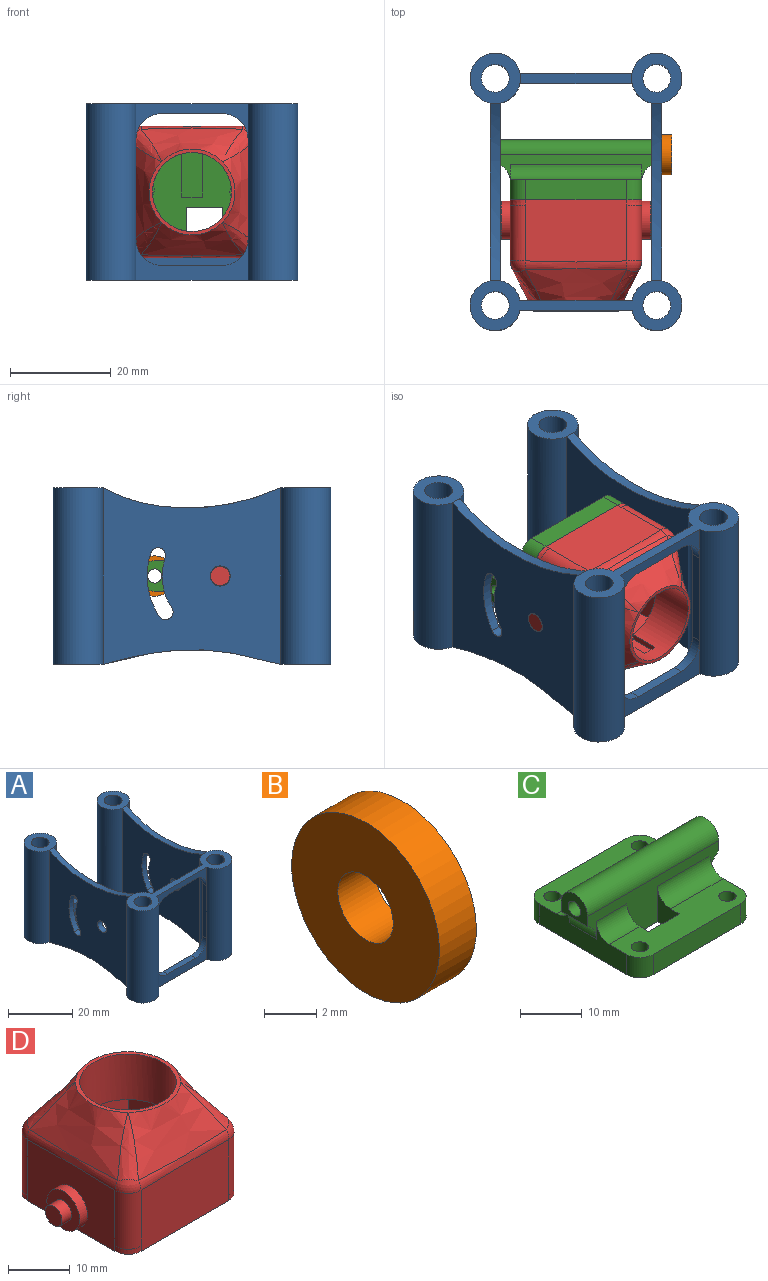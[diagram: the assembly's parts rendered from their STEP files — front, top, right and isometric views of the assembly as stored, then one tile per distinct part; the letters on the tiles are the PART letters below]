
ASSEMBLY  parts=4 mates=5
PART A: 48 faces, bbox 42x55x35 mm
  f0: plane 35.2x35mm, normal (1,0,0), area 1015.3mm2, adj f14,f16,f33,f34,f35,f40,f42,f44
  f1: plane 10x9.9mm, normal (0,0,1), area 54.6mm2, adj f15,f23,f43
  f2: plane 10x9.9mm, normal (0,0,1), area 54.6mm2, adj f16,f20,f42
  f3: plane 42x9.9mm, normal (0,0,1), area 153.4mm2, adj f12,f13,f14,f17,f18,f19,f21,f22
  f4: plane 35.2x35mm, normal (-1,0,0), area 1015.3mm2, adj f12,f15,f36,f37,f38,f41,f43,f46
  f5: plane 35.2x35mm, normal (1,0,0), area 1015.3mm2, adj f15,f22,f36,f37,f38,f41,f43,f46
  f6: plane 35.2x35mm, normal (-1,0,0), area 1015.3mm2, adj f16,f17,f33,f34,f35,f40,f42,f44
  f7: plane 42x9.9mm, normal (0,0,-1), area 153.4mm2, adj f8,f9,f15,f16,f20,f23,f40,f41
  f8: plane 22.2x5mm, normal (0,1,0), area 111mm2, adj f7,f15,f16,f39
  f9: plane 22.2x5mm, normal (0,-1,0), area 111mm2, adj f7,f15,f16,f39
  f10: plane 22.2x8mm, normal (0,-1,0), area 77.3mm2, adj f12,f14,f24,f28,f29,f30
  f11: plane 22.2x8mm, normal (0,1,0), area 77.3mm2, adj f17,f22,f24,f28,f29,f30
  f12: cylinder r=5mm len=35mm, axis (0,0,-1), area 754.2mm2, adj f3,f4,f10,f13,f24,f25
  f13: plane 22.2x7mm, normal (0,-1,0), area 55.1mm2, adj f3,f12,f14,f26,f27,f32
  f14: cylinder r=5mm len=35mm, axis (0,0,-1), area 754.2mm2, adj f0,f3,f10,f13,f24,f31
  f15: cylinder r=5mm len=35mm, axis (0,0,-1), area 1019mm2, adj f1,f4,f5,f7,f8,f9,f39
  f16: cylinder r=5mm len=35mm, axis (0,0,-1), area 1019mm2, adj f0,f2,f6,f7,f8,f9,f39
  f17: cylinder r=5mm len=35mm, axis (0,0,-1), area 204.4mm2, adj f3,f6,f11,f18,f24,f31
  f18: plane 22.2x7mm, normal (0,1,0), area 55.1mm2, adj f3,f17,f22,f26,f27,f32
  f19: cylinder r=2.75mm len=35mm, axis (0,0,-1), area 604.8mm2, adj f3,f24
  f20: cylinder r=2.75mm len=35mm, axis (0,0,-1), area 604.8mm2, adj f2,f7
  f21: cylinder r=2.75mm len=35mm, axis (0,0,-1), area 604.8mm2, adj f3,f24
  f22: cylinder r=5mm len=35mm, axis (0,0,-1), area 204.4mm2, adj f3,f5,f11,f18,f24,f25
  f23: cylinder r=2.75mm len=35mm, axis (0,0,-1), area 604.8mm2, adj f1,f7
  f24: plane 42x9.9mm, normal (0,0,-1), area 153.4mm2, adj f10,f11,f12,f14,f17,f19,f21,f22
  f25: plane 20x2mm, normal (1,0,0), area 40mm2, adj f12,f22,f27,f28
  f26: plane 12.2x2mm, normal (0,0,-1), area 24.4mm2, adj f13,f18,f27,f32
  f27: cylinder r=5mm len=5mm, axis (0,-1,0), area 15.7mm2, adj f13,f18,f25,f26
  f28: cylinder r=5mm len=5mm, axis (0,-1,0), area 15.7mm2, adj f10,f11,f25,f29
  f29: plane 12.2x2mm, normal (0,0,1), area 24.4mm2, adj f10,f11,f28,f30
  f30: cylinder r=5mm len=5mm, axis (0,-1,0), area 15.7mm2, adj f10,f11,f29,f31
  f31: plane 20x2mm, normal (-1,0,0), area 40mm2, adj f14,f17,f30,f32
  f32: cylinder r=5mm len=5mm, axis (0,-1,0), area 15.7mm2, adj f13,f18,f26,f31
  f33: cylinder r=14.5mm len=12.55mm, axis (1,0,0), area 26.2mm2, adj f0,f6,f44,f45
  f34: cylinder r=11.5mm len=9.95mm, axis (1,0,0), area 20.8mm2, adj f0,f6,f44,f45
  f35: cylinder r=2mm len=4mm, axis (1,0,0), area 25.1mm2, adj f0,f6
  f36: cylinder r=11.5mm len=9.95mm, axis (1,0,0), area 20.8mm2, adj f4,f5,f46,f47
  f37: cylinder r=14.5mm len=12.55mm, axis (1,0,0), area 26.2mm2, adj f4,f5,f46,f47
  f38: cylinder r=2mm len=4mm, axis (1,0,0), area 25.1mm2, adj f4,f5
  f39: plane 22.2x2mm, normal (0,0,1), area 44.1mm2, adj f8,f9,f15,f16
  f40: extruded ~35.2x2.91mm, area 71.6mm2, adj f0,f6,f7,f24
  f41: extruded ~35.2x2.91mm, area 71.6mm2, adj f4,f5,f7,f24
  f42: extruded ~35.2x4.01mm, area 72.9mm2, adj f0,f2,f3,f6
  f43: extruded ~35.2x4.01mm, area 72.9mm2, adj f1,f3,f4,f5
  f44: cylinder r=1.5mm len=2.75mm, axis (1,0,0), area 9.4mm2, adj f0,f6,f33,f34
  f45: cylinder r=1.5mm len=2.92mm, axis (1,0,0), area 9.4mm2, adj f0,f6,f33,f34
  f46: cylinder r=1.5mm len=2.75mm, axis (1,0,0), area 9.4mm2, adj f4,f5,f36,f37
  f47: cylinder r=1.5mm len=2.92mm, axis (1,0,0), area 9.4mm2, adj f4,f5,f36,f37
PART B: 4 faces, bbox 2x8x8 mm
  f0: cylinder r=1.5mm len=3mm, axis (-1,0,0), area 18.8mm2, adj f2,f3
  f1: cylinder r=4mm len=8mm, axis (-1,0,0), area 50.3mm2, adj f2,f3
  f2: plane 8x8mm, normal (1,0,0), area 43.2mm2, adj f0,f1
  f3: plane 8x8mm, normal (-1,0,0), area 43.2mm2, adj f0,f1
PART C: 38 faces, bbox 30x26x12 mm
  f0: plane 26x7mm, normal (0,0,1), area 151.8mm2, adj f3,f7,f8,f9,f10,f12,f13,f16
  f1: plane 26x26mm, normal (0,0,-1), area 533.4mm2, adj f3,f4,f5,f6,f7,f8,f9,f10
  f2: plane 26x7mm, normal (0,0,1), area 165.8mm2, adj f3,f4,f5,f6,f7,f11,f14,f30
  f3: plane 20x7mm, normal (1,0,0), area 81.1mm2, adj f0,f1,f2,f4,f10,f15,f28,f30
  f4: cylinder r=3mm len=4mm, axis (0,0,-1), area 18.8mm2, adj f1,f2,f3,f5
  f5: plane 20x4mm, normal (0,1,0), area 80mm2, adj f1,f2,f4,f6
  f6: cylinder r=3mm len=4mm, axis (0,0,-1), area 18.8mm2, adj f1,f2,f5,f7
  f7: plane 20x7mm, normal (-1,0,0), area 81.1mm2, adj f0,f1,f2,f6,f8,f15,f28,f29
  f8: cylinder r=3mm len=4mm, axis (0,0,-1), area 18.8mm2, adj f0,f1,f7,f9
  f9: plane 20x4mm, normal (0,-1,0), area 80mm2, adj f0,f1,f8,f10
  f10: cylinder r=3mm len=4mm, axis (0,0,-1), area 18.8mm2, adj f0,f1,f3,f9
  f11: cylinder r=1.4mm len=4mm, axis (0,0,1), area 35.2mm2, adj f1,f2
  f12: cylinder r=1.4mm len=4mm, axis (0,0,1), area 35.2mm2, adj f0,f1
  f13: cylinder r=1.4mm len=4mm, axis (0,0,1), area 35.2mm2, adj f0,f1
  f14: cylinder r=1.4mm len=4mm, axis (0,0,1), area 35.2mm2, adj f1,f2
  f15: plane 30x8.99mm, normal (0,-1,0), area 112.7mm2, adj f1,f3,f7,f16,f18,f29,f31,f32
  f16: plane 7x5mm, normal (1,0,0), area 21.9mm2, adj f0,f1,f15,f17,f29
  f17: plane 7x4mm, normal (0,1,0), area 28mm2, adj f0,f1,f16,f18
  f18: plane 7x5mm, normal (-1,0,0), area 21.9mm2, adj f0,f1,f15,f17,f31
  f19: cylinder r=2.5mm len=5mm, axis (0,0,-1), area 31.4mm2, adj f1,f20
  f20: plane 5x5mm, normal (0,0,-1), area 19.6mm2, adj f19
  f21: cylinder r=2.5mm len=5mm, axis (0,0,-1), area 31.4mm2, adj f1,f22
  f22: plane 5x5mm, normal (0,0,-1), area 19.6mm2, adj f21
  f23: plane 4x1mm, normal (0,-1,0), area 4mm2, adj f1,f24,f26,f27
  f24: plane 9x1mm, normal (-1,0,0), area 9mm2, adj f1,f23,f25,f27
  f25: plane 4x1mm, normal (0,1,0), area 4mm2, adj f1,f24,f26,f27
  f26: plane 9x1mm, normal (1,0,0), area 9mm2, adj f1,f23,f25,f27
  f27: plane 9x4mm, normal (0,0,-1), area 36mm2, adj f23,f24,f25,f26
  f28: plane 30x5.45mm, normal (0,1,0), area 63.7mm2, adj f3,f7,f30,f32,f33,f34,f35,f36
  f29: cylinder r=3mm len=7mm, axis (1,0,0), area 33mm2, adj f0,f7,f15,f16
  f30: cylinder r=3mm len=26mm, axis (-1,0,0), area 122.5mm2, adj f2,f3,f7,f28
  f31: cylinder r=3mm len=12mm, axis (1,0,0), area 56.5mm2, adj f0,f3,f15,f18
  f32: cylinder r=3mm len=30mm, axis (1,0,0), area 282.7mm2, adj f15,f28,f33,f34
  f33: plane 6x4.99mm, normal (-1,0,0), area 19.9mm2, adj f15,f28,f32,f36,f37
  f34: plane 6x4.99mm, normal (1,0,0), area 19.9mm2, adj f15,f28,f32,f35,f37
  f35: cylinder r=4mm len=6mm, axis (0,-1,0), area 25.1mm2, adj f3,f15,f28,f34
  f36: cylinder r=4mm len=6mm, axis (0,1,0), area 25.1mm2, adj f7,f15,f28,f33
  f37: cylinder r=1.4mm len=30mm, axis (1,0,0), area 263.9mm2, adj f33,f34
PART D: 66 faces, bbox 34x26x22 mm
  f0: plane 26x26mm, normal (0,0,-1), area 288.8mm2, adj f3,f4,f6,f7,f8,f9,f10,f12
  f1: plane 25.1x18mm, normal (0,0,-1), area 159.3mm2, adj f3,f4,f5,f6,f7,f8,f9,f10
  f2: sphere r=3mm, area 8mm2, adj f16,f19,f20,f21
  f3: plane 13x6.38mm, normal (1,0,0), area 82.9mm2, adj f0,f1,f4,f14
  f4: plane 13x0.88mm, normal (0,-1,0), area 11.4mm2, adj f0,f1,f3,f5,f44
  f5: cylinder r=2.62mm len=12mm, axis (0,0,1), area 99mm2, adj f1,f4,f6,f44
  f6: plane 13x0.88mm, normal (0,1,0), area 11.4mm2, adj f0,f1,f5,f7,f44
  f7: plane 13x6.38mm, normal (1,0,0), area 82.9mm2, adj f0,f1,f6,f8
  f8: plane 18x13mm, normal (0,1,0), area 234mm2, adj f0,f1,f7,f9
  f9: plane 13x6.38mm, normal (-1,0,0), area 82.9mm2, adj f0,f1,f8,f10
  f10: plane 13x0.88mm, normal (0,1,0), area 11.4mm2, adj f0,f1,f9,f11,f45
  f11: cylinder r=2.62mm len=12mm, axis (0,0,1), area 99mm2, adj f1,f10,f12,f45
  f12: plane 13x0.88mm, normal (0,-1,0), area 11.4mm2, adj f0,f1,f11,f13,f45
  f13: plane 13x6.38mm, normal (-1,0,0), area 82.9mm2, adj f0,f1,f12,f14
  f14: plane 18x13mm, normal (0,-1,0), area 234mm2, adj f0,f1,f3,f13
  f15: plane 20x12.29mm, normal (0,1,0), area 244.3mm2, adj f0,f16,f21,f22,f48,f49
  f16: cylinder r=3mm len=11.07mm, axis (0,0,-1), area 52.2mm2, adj f2,f15,f17,f49
  f17: plane 20x12.29mm, normal (1,0,0), area 200.1mm2, adj f0,f16,f18,f19,f46,f49,f50
  f18: cylinder r=3mm len=11.07mm, axis (0,0,-1), area 52.2mm2, adj f17,f23,f24,f46
  f19: bspline ~20.54x1.74mm, area 31mm2, adj f2,f17,f23,f26
  f20: bspline ~8.2x6.44mm, area 15.1mm2, adj f2,f26,f27
  f21: bspline ~20.54x1.74mm, area 31mm2, adj f2,f15,f27,f29
  f22: cylinder r=3mm len=11.07mm, axis (0,0,-1), area 52.2mm2, adj f15,f28,f29,f48
  f23: sphere r=3mm, area 8mm2, adj f18,f19,f30,f32
  f24: plane 20x12.29mm, normal (0,-1,0), area 244.3mm2, adj f0,f18,f31,f32,f46,f47
  f25: cylinder r=7.83mm len=15.65mm, axis (0,0,-1), area 424.4mm2, adj f1,f33,f40,f41,f42
  f26: bspline ~25.15x8.45mm, area 164.2mm2, adj f19,f20,f30,f33
  f27: bspline ~24.76x8.2mm, area 164.2mm2, adj f20,f21,f33,f34
  f28: plane 20x12.29mm, normal (-1,0,0), area 200.1mm2, adj f0,f22,f31,f35,f47,f48,f54
  f29: sphere r=3mm, area 8mm2, adj f21,f22,f34,f35
  f30: bspline ~8.2x6.44mm, area 15.1mm2, adj f23,f26,f36
  f31: cylinder r=3mm len=11.07mm, axis (0,0,-1), area 52.2mm2, adj f24,f28,f37,f47
  f32: bspline ~20.54x1.74mm, area 31mm2, adj f23,f24,f36,f37
  f33: plane 17.32x17.32mm, normal (0,0,1), area 34.6mm2, adj f25,f26,f27,f36,f38
  f34: revolved ~8.21x7.88mm, area 20mm2, adj f27,f29,f38
  f35: bspline ~20.54x1.74mm, area 31mm2, adj f28,f29,f37,f38
  f36: bspline ~25.15x8.45mm, area 164.2mm2, adj f30,f32,f33,f39
  f37: sphere r=3mm, area 8mm2, adj f31,f32,f35,f39
  f38: bspline ~24.76x8.2mm, area 164.2mm2, adj f33,f34,f35,f39
  f39: revolved ~8.21x7.88mm, area 20mm2, adj f36,f37,f38
  f40: plane 6x1.15mm, normal (-1,0,0), area 6.9mm2, adj f1,f25,f42,f43
  f41: plane 6x1.15mm, normal (1,0,0), area 6.9mm2, adj f1,f25,f42,f43
  f42: plane 3x1.15mm, normal (0,0,-1), area 3.1mm2, adj f25,f40,f41,f43
  f43: plane 6x3mm, normal (0,1,0), area 18mm2, adj f1,f40,f41,f42
  f44: extruded ~5.25x2.63mm, area 8.2mm2, adj f0,f4,f5,f6
  f45: extruded ~5.25x2.63mm, area 8.2mm2, adj f0,f10,f11,f12
  f46: extruded ~3x3mm, area 4.7mm2, adj f0,f17,f18,f24
  f47: extruded ~3x3mm, area 4.7mm2, adj f0,f24,f28,f31
  f48: extruded ~3x3mm, area 4.7mm2, adj f0,f15,f22,f28
  f49: extruded ~3x3mm, area 4.7mm2, adj f0,f15,f16,f17
  f50: cylinder r=3.75mm len=7.5mm, axis (-1,0,0), area 42.4mm2, adj f17,f51
  f51: plane 7.5x7.5mm, normal (1,0,0), area 32.8mm2, adj f50,f53
  f52: plane 3.8x3.8mm, normal (1,0,0), area 11.3mm2, adj f53
  f53: cylinder r=1.9mm len=3.8mm, axis (-1,0,0), area 26.3mm2, adj f51,f52
  f54: cylinder r=3.75mm len=7.5mm, axis (1,0,0), area 42.4mm2, adj f28,f55
  f55: plane 7.5x7.5mm, normal (-1,0,0), area 32.8mm2, adj f54,f57
  f56: plane 3.8x3.8mm, normal (-1,0,0), area 11.3mm2, adj f57
  f57: cylinder r=1.9mm len=3.8mm, axis (1,0,0), area 26.3mm2, adj f55,f56
  f58: cylinder r=1.4mm len=10mm, axis (0,0,-1), area 88mm2, adj f0,f59
  f59: plane 2.8x2.8mm, normal (0,0,-1), area 6.2mm2, adj f58
  f60: cylinder r=1.4mm len=10mm, axis (0,0,-1), area 88mm2, adj f0,f61
  f61: plane 2.8x2.8mm, normal (0,0,-1), area 6.2mm2, adj f60
  f62: cylinder r=1.4mm len=10mm, axis (0,0,-1), area 88mm2, adj f0,f63
  f63: plane 2.8x2.8mm, normal (0,0,-1), area 6.2mm2, adj f62
  f64: cylinder r=1.4mm len=10mm, axis (0,0,-1), area 88mm2, adj f0,f65
  f65: plane 2.8x2.8mm, normal (0,0,-1), area 6.2mm2, adj f64
PLACE A t=(1.71,45.47,-17.63)mm
PLACE B t=(16.55,51.13,-0.13)mm
PLACE C rot(axis=(0,-0.71,-0.71),180deg) t=(12.55,42.13,-13.13)mm
PLACE D rot(axis=(1,0,0),90deg) t=(-0.45,29.13,-0.13)mm
MATE cylindrical B.f0 <-> C.f37  axis (-1,0,0) through (16.55,51.13,-0.13)mm
MATE cylindrical D.f16 <-> C.f6  axis (0,1,0) through (9.55,42.13,9.87)mm
MATE planar B.f1 <-> A.f0  axis (-1,0,0) through (16.55,51.13,-0.13)mm
MATE cylindrical D.f50 <-> A.f33  axis (-1,0,0) through (15.45,38.13,-0.13)mm
MATE planar D.f16 <-> C.f6  axis (0,1,0) through (9.55,42.13,9.87)mm
